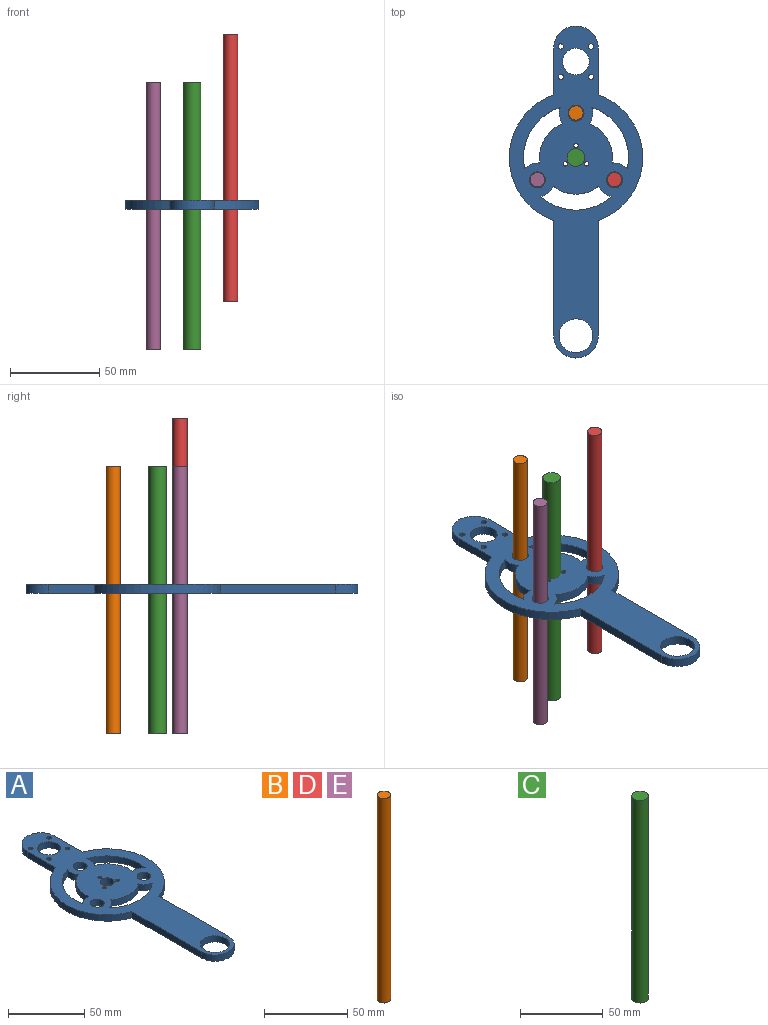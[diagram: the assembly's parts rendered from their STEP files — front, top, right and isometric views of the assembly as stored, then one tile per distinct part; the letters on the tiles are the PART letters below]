
ASSEMBLY  parts=5 mates=4
PART A: 35 faces, bbox 75x186.4x5 mm
  f0: cylinder r=9.5mm len=8.56mm, axis (0,0,-1), area 47.6mm2, adj f1,f22,f33,f34
  f1: cylinder r=29.5mm len=34.37mm, axis (0,0,-1), area 217.7mm2, adj f0,f2,f33,f34
  f2: cylinder r=9.5mm len=9mm, axis (0,0,-1), area 47.6mm2, adj f1,f22,f33,f34
  f3: cylinder r=29.5mm len=39.69mm, axis (0,0,-1), area 217.7mm2, adj f4,f23,f33,f34
  f4: cylinder r=9.5mm len=7.03mm, axis (0,0,-1), area 47.6mm2, adj f3,f5,f33,f34
  f5: cylinder r=20.5mm len=25.64mm, axis (0,0,-1), area 138.5mm2, adj f4,f23,f33,f34
  f6: cylinder r=29.5mm len=34.37mm, axis (0,0,-1), area 217.7mm2, adj f7,f24,f33,f34
  f7: cylinder r=9.5mm len=8.56mm, axis (0,0,-1), area 47.6mm2, adj f6,f8,f33,f34
  f8: cylinder r=20.5mm len=22.2mm, axis (0,0,-1), area 138.5mm2, adj f7,f24,f33,f34
  f9: plane 64.64x5mm, normal (1,0,0), area 323.2mm2, adj f10,f30,f33,f34
  f10: cylinder r=37.5mm len=70.71mm, axis (0,0,-1), area 461.6mm2, adj f9,f11,f33,f34
  f11: plane 26.07x5mm, normal (1,0,0), area 130.3mm2, adj f10,f12,f33,f34
  f12: cylinder r=12.5mm len=25mm, axis (0,0,-1), area 196.3mm2, adj f11,f13,f33,f34
  f13: plane 26.07x5mm, normal (-1,0,0), area 130.3mm2, adj f12,f14,f33,f34
  f14: cylinder r=37.5mm len=70.71mm, axis (0,0,-1), area 461.6mm2, adj f13,f15,f33,f34
  f15: plane 64.64x5mm, normal (-1,0,0), area 323.2mm2, adj f14,f30,f33,f34
  f16: cylinder r=4.5mm len=9mm, axis (0,0,-1), area 141.4mm2, adj f33,f34
  f17: cylinder r=4.5mm len=9mm, axis (0,0,-1), area 141.4mm2, adj f33,f34
  f18: cylinder r=1.25mm len=5mm, axis (0,0,-1), area 39.3mm2, adj f33,f34
  f19: cylinder r=1.25mm len=5mm, axis (0,0,-1), area 39.3mm2, adj f33,f34
  f20: cylinder r=1.25mm len=5mm, axis (0,0,-1), area 39.3mm2, adj f33,f34
  f21: cylinder r=4.5mm len=9mm, axis (0,0,-1), area 141.4mm2, adj f33,f34
  f22: cylinder r=20.5mm len=22.2mm, axis (0,0,-1), area 138.5mm2, adj f0,f2,f33,f34
  f23: cylinder r=9.5mm len=7.03mm, axis (0,0,-1), area 47.6mm2, adj f3,f5,f33,f34
  f24: cylinder r=9.5mm len=9mm, axis (0,0,-1), area 47.6mm2, adj f6,f8,f33,f34
  f25: cylinder r=1.5mm len=5mm, axis (0,0,-1), area 47.1mm2, adj f33,f34
  f26: cylinder r=1.5mm len=5mm, axis (0,0,-1), area 47.1mm2, adj f33,f34
  f27: cylinder r=7.5mm len=15mm, axis (0,0,-1), area 235.6mm2, adj f33,f34
  f28: cylinder r=1.5mm len=5mm, axis (0,0,-1), area 47.1mm2, adj f33,f34
  f29: cylinder r=1.5mm len=5mm, axis (0,0,-1), area 47.1mm2, adj f33,f34
  f30: cylinder r=12.5mm len=25mm, axis (0,0,-1), area 196.3mm2, adj f9,f15,f33,f34
  f31: cylinder r=9.5mm len=19mm, axis (0,0,-1), area 298.5mm2, adj f33,f34
  f32: cylinder r=4.5mm len=9mm, axis (0,0,-1), area 141.4mm2, adj f33,f34
  f33: plane 186.42x75mm, normal (0,0,1), area 5428.4mm2, adj f0,f1,f2,f3,f4,f5,f6,f7
  f34: plane 186.42x75mm, normal (0,0,-1), area 5428.4mm2, adj f0,f1,f2,f3,f4,f5,f6,f7
PART B: 3 faces, bbox 8x8x150 mm
  f0: cylinder r=4mm len=150mm, axis (0,0,-1), area 3769.9mm2, adj f1,f2
  f1: plane 8x8mm, normal (0,0,1), area 50.3mm2, adj f0
  f2: plane 8x8mm, normal (0,0,-1), area 50.3mm2, adj f0
PART C: 3 faces, bbox 10x10x150 mm
  f0: cylinder r=5mm len=150mm, axis (0,0,-1), area 4712.4mm2, adj f1,f2
  f1: plane 10x10mm, normal (0,0,1), area 78.5mm2, adj f0
  f2: plane 10x10mm, normal (0,0,-1), area 78.5mm2, adj f0
PART D: same geometry as B
PART E: same geometry as B
PLACE A t=(0,0,-71.04)mm
PLACE B t=(0,25,-75.07)mm
PLACE C t=(0,0,-75)mm
PLACE D t=(21.65,-12.5,-47.75)mm
PLACE E t=(-21.65,-12.5,-74.94)mm
MATE slider E.f0 <-> A.f0  axis (0,0,-1) through (-21.65,-12.5,-74.94)mm
MATE slider C.f0 <-> A.f1  axis (0,0,-1) through (0,0,-75)mm
MATE slider B.f0 <-> A.f2  axis (0,0,-1) through (0,25,-75.07)mm
MATE slider D.f0 <-> A.f7  axis (0,0,-1) through (21.65,-12.5,-47.75)mm
